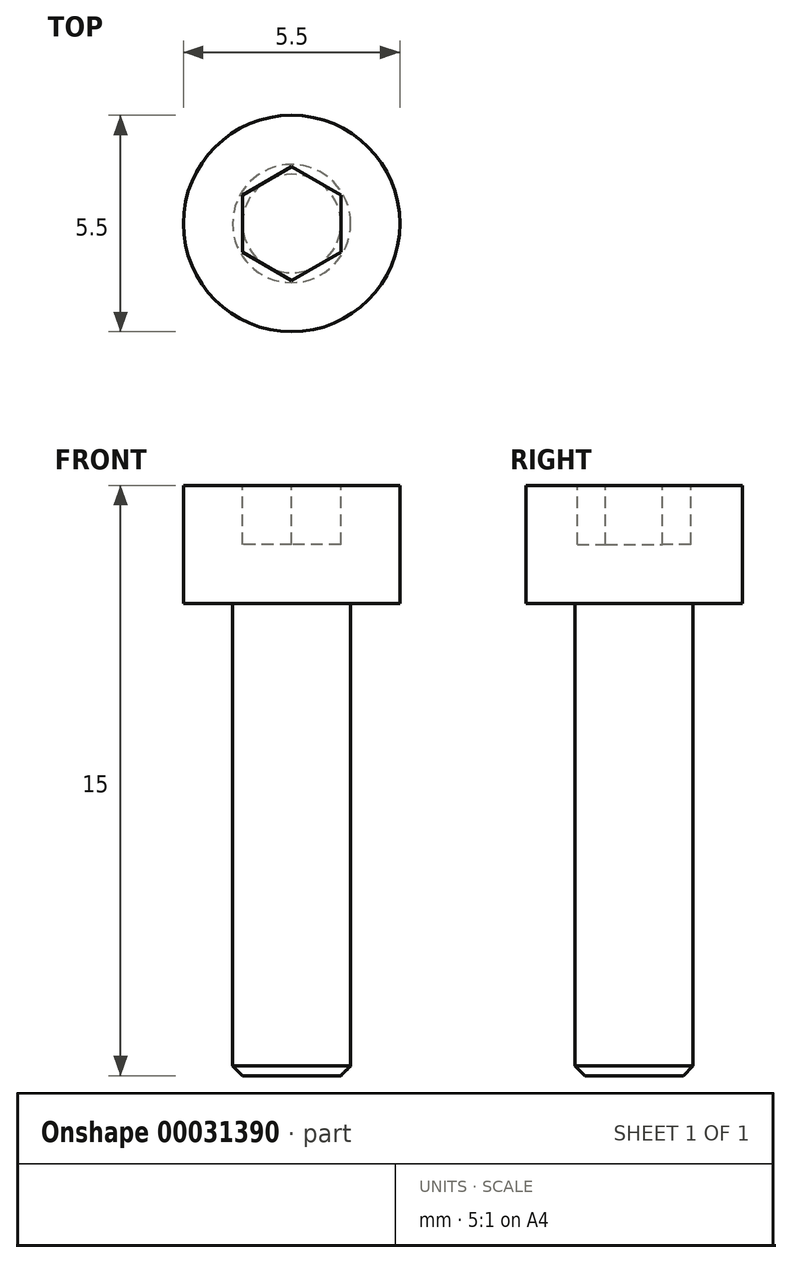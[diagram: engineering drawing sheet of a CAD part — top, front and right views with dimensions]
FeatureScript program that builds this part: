
annotation { "Feature Type Name" : "Feature", "Feature Type Description" : "" }
export const myFeature = defineFeature(function(context is Context, id is Id, definition is map)
    precondition{}
    {
        {
            var Q0;
            Q0=qCreatedBy(makeId("Front.planeOp"),FACE);
            var sketch = newSketch(context, id + "F0", { "sketchPlane" : qUnion([Q0])});
            skLineSegment(sketch, "E0", {"start": v(0, 0) * mm, "end": v(-1.5, 0) * mm});
            skLineSegment(sketch, "E1", {"start": v(-1.5, 0) * mm, "end": v(-1.5, 12) * mm});
            skLineSegment(sketch, "E2", {"start": v(-1.5, 12) * mm, "end": v(-2.75, 12) * mm});
            skLineSegment(sketch, "E3", {"start": v(-2.75, 12) * mm, "end": v(-2.75, 15) * mm});
            skLineSegment(sketch, "E4", {"start": v(-2.75, 15) * mm, "end": v(0, 15) * mm});
            skLineSegment(sketch, "E5", {"start": v(0, 15) * mm, "end": v(0, 0) * mm});
            skLineSegment(sketch, "E6", {"start": v(0, 0) * mm, "end": v(0, -5.02) * mm, "construction": true});
            skSolve(sketch);
        }
        {
            var Q0;
            Q0=makeQuery(id+"F0.imprint","IMPRINT",FACE,{"disambiguationData":[TD([[makeQuery(id+"F0.imprint","IMPRINT",EDGE,{"derivedFrom":sQuery(id+"F0.wireOp",EDGE,"E0")}),-1.0]])]});
            var Q1;
            Q1=sQuery(id+"F0.wireOp",EDGE,"E6");
            revolve(context, id + "F1", {"entities" : qUnion([Q0]), "axis" : qUnion([Q1]), "revolveType" : RevolveType.FULL});
        }
        {
            var Q0;
            Q0=makeQuery(id+"F1.opRevolve","SWEPT_FACE",FACE,{"disambiguationData":[OSD([sQuery(id+"F0.wireOp",EDGE,"E4")])]});
            var sketch = newSketch(context, id + "F2", { "sketchPlane" : qUnion([Q0])});
            skCircle(sketch, "E7.cCircle", {"center": v(0, 0) * mm, "radius": 1.25 * mm, "construction": true});
            skLineSegment(sketch, "E7.0", {"start": v(-1.25, -0.72) * mm, "end": v(-1.25, 0.72) * mm});
            skLineSegment(sketch, "E7.1", {"start": v(-1.25, 0.72) * mm, "end": v(0, 1.44) * mm});
            skLineSegment(sketch, "E7.2", {"start": v(0, 1.44) * mm, "end": v(1.25, 0.72) * mm});
            skLineSegment(sketch, "E7.3", {"start": v(1.25, 0.72) * mm, "end": v(1.25, -0.72) * mm});
            skLineSegment(sketch, "E7.4", {"start": v(1.25, -0.72) * mm, "end": v(0, -1.44) * mm});
            skLineSegment(sketch, "E7.5", {"start": v(0, -1.44) * mm, "end": v(-1.25, -0.72) * mm});
            skPoint(sketch, "E7.0.midPoint", {"position": v(-1.25, 0) * mm});
            skSolve(sketch);
        }
        {
            var Q0;
            Q0 = qSketchRegion(id + "F2", true);
            var Q1;
            Q1=makeQuery(id+"F2.imprint","IMPRINT",FACE,{"disambiguationData":[TD([[makeQuery(id+"F2.imprint","IMPRINT",EDGE,{"derivedFrom":sQuery(id+"F2.wireOp",EDGE,"E7.0")}),-1.0]])]});
            extrude(context, id + "F3", {"entities" : qUnion([Q0, Q1]), "operationType" : NewBodyOperationType.REMOVE, "oppositeDirection" : true, "depth" : 1.5 * mm});
        }
        {
            var Q0;
            Q0=makeQuery(id+"F1.opRevolve","SWEPT_EDGE",EDGE,{"disambiguationData":[OSD([sQuery(id+"F0.wireOp",EDGE,"E0"),sQuery(id+"F0.wireOp",EDGE,"E1")])]});
            chamfer(context, id + "F4", {"entities" : qUnion([Q0]), "width" : 0.25 * mm, "tangentPropagation" : true});
        }
    });
